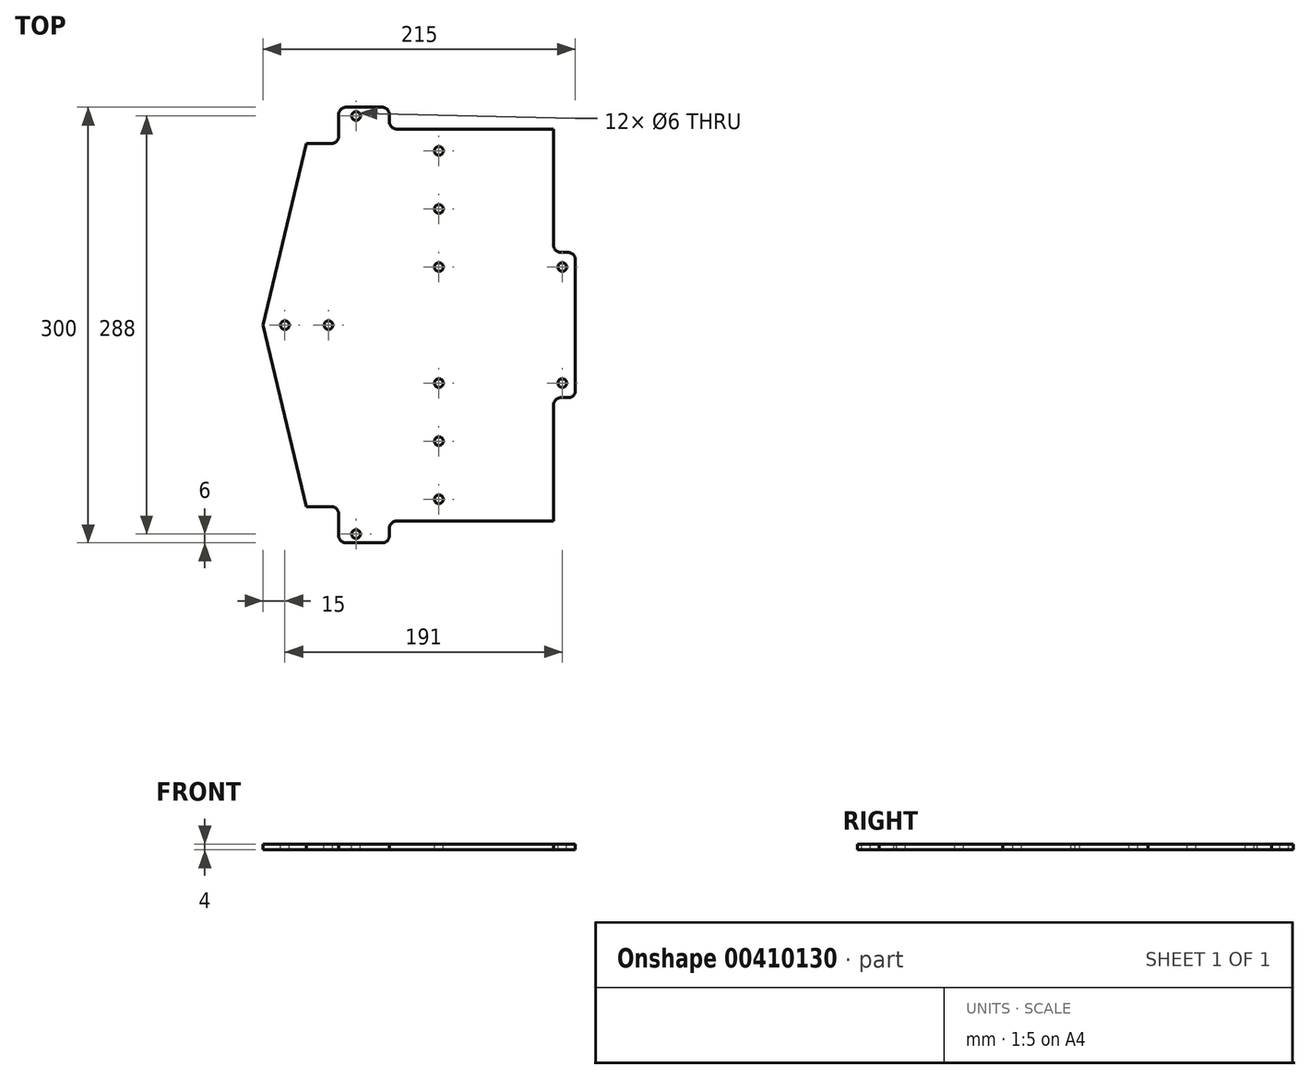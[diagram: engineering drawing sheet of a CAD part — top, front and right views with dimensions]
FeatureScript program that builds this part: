
annotation { "Feature Type Name" : "Feature", "Feature Type Description" : "" }
export const myFeature = defineFeature(function(context is Context, id is Id, definition is map)
    precondition{}
    {
        {
            var Q0;
            Q0=qCreatedBy(makeId("Top.planeOp"),FACE);
            var sketch = newSketch(context, id + "F0", { "sketchPlane" : qUnion([Q0])});
            skLineSegment(sketch, "E0.bottom", {"start": v(0, 0) * mm, "end": v(320, 0) * mm});
            skLineSegment(sketch, "E0.top", {"start": v(0, 420) * mm, "end": v(320, 420) * mm});
            skLineSegment(sketch, "E0.left", {"start": v(0, 0) * mm, "end": v(0, 420) * mm});
            skLineSegment(sketch, "E0.right", {"start": v(320, 0) * mm, "end": v(320, 420) * mm});
            skSolve(sketch);
        }
        {
            var Q0;
            Q0=qSketchRegion(id+"F0",true);
            extrude(context, id + "F1", {"entities" : qUnion([Q0]), "depth" : 4 * mm});
        }
        {
            var Q0;
            Q0=makeQuery(id+"F1.opExtrude","CAP_FACE",FACE,{"disambiguationData":[OSD([sQuery(id+"F0.wireOp",EDGE,"E0.bottom"),sQuery(id+"F0.wireOp",EDGE,"E0.top"),sQuery(id+"F0.wireOp",EDGE,"E0.left"),sQuery(id+"F0.wireOp",EDGE,"E0.right")])],"isStart":false});
            var sketch = newSketch(context, id + "F2", { "sketchPlane" : qUnion([Q0])});
            skLineSegment(sketch, "E1", {"start": v(290, 420) * mm, "end": v(320, 360) * mm});
            skLineSegment(sketch, "E2", {"start": v(290, 420) * mm, "end": v(320, 420) * mm});
            skLineSegment(sketch, "E3", {"start": v(320, 420) * mm, "end": v(320, 360) * mm});
            skLineSegment(sketch, "E4", {"start": v(290, 0) * mm, "end": v(320, 60) * mm});
            skLineSegment(sketch, "E5", {"start": v(290, 0) * mm, "end": v(320, 0) * mm});
            skLineSegment(sketch, "E6", {"start": v(320, 0) * mm, "end": v(320, 60) * mm});
            skLineSegment(sketch, "E7", {"start": v(0, 210) * mm, "end": v(320, 210) * mm, "construction": true});
            skLineSegment(sketch, "E8", {"start": v(163, 384) * mm, "end": v(163, 36) * mm, "construction": true});
            skPoint(sketch, "E9", {"position": v(163, 210) * mm});
            skLineSegment(sketch, "E10.bottom", {"start": v(213, 360) * mm, "end": v(113, 360) * mm});
            skLineSegment(sketch, "E10.top", {"start": v(213, 408) * mm, "end": v(113, 408) * mm});
            skLineSegment(sketch, "E10.left", {"start": v(218, 365) * mm, "end": v(218, 403) * mm});
            skLineSegment(sketch, "E10.right", {"start": v(108, 365) * mm, "end": v(108, 403) * mm});
            skPoint(sketch, "E10.middle", {"position": v(163, 384) * mm});
            skLineSegment(sketch, "E11.bottom", {"start": v(213, 12) * mm, "end": v(113, 12) * mm});
            skLineSegment(sketch, "E11.top", {"start": v(213, 60) * mm, "end": v(113, 60) * mm});
            skLineSegment(sketch, "E11.left", {"start": v(218, 17) * mm, "end": v(218, 55) * mm});
            skLineSegment(sketch, "E11.right", {"start": v(108, 17) * mm, "end": v(108, 55) * mm});
            skPoint(sketch, "E11.middle", {"position": v(163, 36) * mm});
            skPoint(sketch, "E12.visualSharp", {"position": v(108, 408) * mm});
            skArc(sketch, "E12.filletArc", {"start": v(113, 408) * mm, "mid": v(109.46, 406.54) * mm, "end": v(108, 403) * mm});
            skPoint(sketch, "E13.visualSharp", {"position": v(218, 408) * mm});
            skArc(sketch, "E13.filletArc", {"start": v(218, 403) * mm, "mid": v(216.54, 406.54) * mm, "end": v(213, 408) * mm});
            skPoint(sketch, "E14.visualSharp", {"position": v(108, 360) * mm});
            skArc(sketch, "E14.filletArc", {"start": v(108, 365) * mm, "mid": v(109.46, 361.46) * mm, "end": v(113, 360) * mm});
            skPoint(sketch, "E15.visualSharp", {"position": v(218, 360) * mm});
            skArc(sketch, "E15.filletArc", {"start": v(213, 360) * mm, "mid": v(216.54, 361.46) * mm, "end": v(218, 365) * mm});
            skPoint(sketch, "E16.visualSharp", {"position": v(218, 60) * mm});
            skArc(sketch, "E16.filletArc", {"start": v(218, 55) * mm, "mid": v(216.54, 58.54) * mm, "end": v(213, 60) * mm});
            skPoint(sketch, "E17.visualSharp", {"position": v(218, 12) * mm});
            skArc(sketch, "E17.filletArc", {"start": v(213, 12) * mm, "mid": v(216.54, 13.46) * mm, "end": v(218, 17) * mm});
            skPoint(sketch, "E18.visualSharp", {"position": v(108, 12) * mm});
            skArc(sketch, "E18.filletArc", {"start": v(108, 17) * mm, "mid": v(109.46, 13.46) * mm, "end": v(113, 12) * mm});
            skPoint(sketch, "E19.visualSharp", {"position": v(108, 60) * mm});
            skArc(sketch, "E19.filletArc", {"start": v(113, 60) * mm, "mid": v(109.46, 58.54) * mm, "end": v(108, 55) * mm});
            skLineSegment(sketch, "E20", {"start": v(0, 210) * mm, "end": v(50, 420) * mm});
            skLineSegment(sketch, "E21", {"start": v(0, 210) * mm, "end": v(50, 0) * mm});
            skLineSegment(sketch, "E22", {"start": v(50, 420) * mm, "end": v(0, 420) * mm});
            skLineSegment(sketch, "E23", {"start": v(0, 420) * mm, "end": v(0, 0) * mm});
            skLineSegment(sketch, "E24", {"start": v(0, 0) * mm, "end": v(50, 0) * mm});
            skSolve(sketch);
        }
        {
            var Q0;
            Q0=qSketchRegion(id+"F2",true);
            var Q1;
            Q1=makeQuery(id+"F1.opExtrude","CAP_FACE",FACE,{"disambiguationData":[OSD([sQuery(id+"F0.wireOp",EDGE,"E0.bottom"),sQuery(id+"F0.wireOp",EDGE,"E0.top"),sQuery(id+"F0.wireOp",EDGE,"E0.left"),sQuery(id+"F0.wireOp",EDGE,"E0.right")])],"isStart":true});
            extrude(context, id + "F3", {"entities" : qUnion([Q0]), "operationType" : NewBodyOperationType.REMOVE, "endBound" : BoundingType.UP_TO_SURFACE, "oppositeDirection" : true, "endBoundEntityFace" : qUnion([Q1]), "depth" : 25 * mm});
        }
        {
            var Q0;
            Q0=makeQuery(id+"F1.opExtrude","CAP_FACE",FACE,{"disambiguationData":[OSD([sQuery(id+"F0.wireOp",EDGE,"E0.bottom"),sQuery(id+"F0.wireOp",EDGE,"E0.top"),sQuery(id+"F0.wireOp",EDGE,"E0.left"),sQuery(id+"F0.wireOp",EDGE,"E0.right")])],"isStart":false});
            var sketch = newSketch(context, id + "F4", { "sketchPlane" : qUnion([Q0])});
            skLineSegment(sketch, "E25", {"start": v(67, 6) * mm, "end": v(277, 6) * mm, "construction": true});
            skCircle(sketch, "E26", {"center": v(67, 6) * mm, "radius": 3 * mm});
            skCircle(sketch, "E27.1.0.0", {"center": v(97, 6) * mm, "radius": 3 * mm});
            skCircle(sketch, "E27.2.0.0", {"center": v(127, 6) * mm, "radius": 3 * mm});
            skCircle(sketch, "E27.3.0.0", {"center": v(157, 6) * mm, "radius": 3 * mm});
            skCircle(sketch, "E27.4.0.0", {"center": v(187, 6) * mm, "radius": 3 * mm});
            skCircle(sketch, "E27.5.0.0", {"center": v(217, 6) * mm, "radius": 3 * mm});
            skCircle(sketch, "E27.6.0.0", {"center": v(247, 6) * mm, "radius": 3 * mm});
            skCircle(sketch, "E27.7.0.0", {"center": v(277, 6) * mm, "radius": 3 * mm});
            skLineSegment(sketch, "E27.direction1", {"start": v(67, 6) * mm, "end": v(97, 6) * mm, "construction": true});
            skLineSegment(sketch, "E28", {"start": v(70, 66) * mm, "end": v(310, 66) * mm, "construction": true});
            skCircle(sketch, "E29", {"center": v(64, 66) * mm, "radius": 3 * mm});
            skCircle(sketch, "E30.1.0.0", {"center": v(94, 66) * mm, "radius": 3 * mm});
            skCircle(sketch, "E30.2.0.0", {"center": v(124, 66) * mm, "radius": 3 * mm});
            skCircle(sketch, "E30.3.0.0", {"center": v(160, 66) * mm, "radius": 3 * mm, "construction": true});
            skCircle(sketch, "E30.4.0.0", {"center": v(190, 66) * mm, "radius": 3 * mm, "construction": true});
            skCircle(sketch, "E30.5.0.0", {"center": v(220, 66) * mm, "radius": 3 * mm});
            skCircle(sketch, "E30.6.0.0", {"center": v(250, 66) * mm, "radius": 3 * mm});
            skCircle(sketch, "E30.7.0.0", {"center": v(280, 66) * mm, "radius": 3 * mm});
            skCircle(sketch, "E30.8.0.0", {"center": v(310, 66) * mm, "radius": 3 * mm});
            skLineSegment(sketch, "E30.direction1", {"start": v(64, 66) * mm, "end": v(94, 66) * mm, "construction": true});
            skLineSegment(sketch, "E31", {"start": v(0, 210) * mm, "end": v(320, 210) * mm, "construction": true});
            skCircle(sketch, "E32.MirrorC", {"center": v(67, 414) * mm, "radius": 3 * mm});
            skCircle(sketch, "E33.MirrorC", {"center": v(64, 354) * mm, "radius": 3 * mm});
            skCircle(sketch, "E34.MirrorC", {"center": v(97, 414) * mm, "radius": 3 * mm});
            skCircle(sketch, "E35.MirrorC", {"center": v(310, 354) * mm, "radius": 3 * mm});
            skCircle(sketch, "E36.MirrorC", {"center": v(277, 414) * mm, "radius": 3 * mm});
            skCircle(sketch, "E37.MirrorC", {"center": v(94, 354) * mm, "radius": 3 * mm});
            skCircle(sketch, "E38.MirrorC", {"center": v(220, 354) * mm, "radius": 3 * mm});
            skLineSegment(sketch, "E39.MirrorCS", {"start": v(64, 354) * mm, "end": v(94, 354) * mm, "construction": true});
            skCircle(sketch, "E40.MirrorC", {"center": v(280, 354) * mm, "radius": 3 * mm});
            skCircle(sketch, "E41.MirrorC", {"center": v(124, 354) * mm, "radius": 3 * mm});
            skCircle(sketch, "E42.MirrorC", {"center": v(160, 354) * mm, "radius": 3 * mm, "construction": true});
            skCircle(sketch, "E43.MirrorC", {"center": v(190, 354) * mm, "radius": 3 * mm, "construction": true});
            skCircle(sketch, "E44.MirrorC", {"center": v(127, 414) * mm, "radius": 3 * mm});
            skCircle(sketch, "E45.MirrorC", {"center": v(250, 354) * mm, "radius": 3 * mm});
            skCircle(sketch, "E46.MirrorC", {"center": v(157, 414) * mm, "radius": 3 * mm});
            skCircle(sketch, "E47.MirrorC", {"center": v(187, 414) * mm, "radius": 3 * mm});
            skCircle(sketch, "E48.MirrorC", {"center": v(217, 414) * mm, "radius": 3 * mm});
            skCircle(sketch, "E49.MirrorC", {"center": v(247, 414) * mm, "radius": 3 * mm});
            skLineSegment(sketch, "E50.MirrorCS", {"start": v(67, 414) * mm, "end": v(277, 414) * mm, "construction": true});
            skLineSegment(sketch, "E51.MirrorCS", {"start": v(67, 414) * mm, "end": v(97, 414) * mm, "construction": true});
            skLineSegment(sketch, "E52.MirrorCS", {"start": v(70, 354) * mm, "end": v(310, 354) * mm, "construction": true});
            skSolve(sketch);
        }
        {
            var Q0;
            Q0=qSketchRegion(id+"F4",true);
            extrude(context, id + "F5", {"entities" : qUnion([Q0]), "operationType" : NewBodyOperationType.REMOVE, "oppositeDirection" : true, "depth" : 25 * mm});
        }
        {
            var Q0;
            Q0=makeQuery(id+"F1.opExtrude","CAP_FACE",FACE,{"disambiguationData":[OSD([sQuery(id+"F0.wireOp",EDGE,"E0.bottom"),sQuery(id+"F0.wireOp",EDGE,"E0.top"),sQuery(id+"F0.wireOp",EDGE,"E0.left"),sQuery(id+"F0.wireOp",EDGE,"E0.right")])],"isStart":false});
            var sketch = newSketch(context, id + "F6", { "sketchPlane" : qUnion([Q0])});
            skLineSegment(sketch, "E53", {"start": v(0, 210) * mm, "end": v(320, 210) * mm, "construction": true});
            skLineSegment(sketch, "E54", {"start": v(108, 365) * mm, "end": v(108, 55) * mm, "construction": true});
            skLineSegment(sketch, "E55", {"start": v(121, 90) * mm, "end": v(121, 330.2) * mm, "construction": true});
            skCircle(sketch, "E56", {"center": v(121, 90) * mm, "radius": 3 * mm});
            skCircle(sketch, "E57.0.1.0", {"center": v(121, 130) * mm, "radius": 3 * mm});
            skCircle(sketch, "E57.0.2.0", {"center": v(121, 170) * mm, "radius": 3 * mm});
            skCircle(sketch, "E57.1.0.0", {"center": v(206, 90) * mm, "radius": 3 * mm});
            skCircle(sketch, "E57.1.1.0", {"center": v(206, 130) * mm, "radius": 3 * mm});
            skCircle(sketch, "E57.1.2.0", {"center": v(206, 170) * mm, "radius": 3 * mm});
            skCircle(sketch, "E57.2.0.0", {"center": v(291, 80) * mm, "radius": 3 * mm});
            skCircle(sketch, "E57.2.1.0", {"center": v(291, 120) * mm, "radius": 3 * mm});
            skCircle(sketch, "E57.2.2.0", {"center": v(291, 160) * mm, "radius": 3 * mm});
            skLineSegment(sketch, "E57.direction1", {"start": v(121, 90) * mm, "end": v(206, 90) * mm, "construction": true});
            skLineSegment(sketch, "E57.direction2", {"start": v(121, 90) * mm, "end": v(121, 130) * mm, "construction": true});
            skCircle(sketch, "E58.MirrorC", {"center": v(121, 330) * mm, "radius": 3 * mm});
            skCircle(sketch, "E59.MirrorC", {"center": v(121, 290) * mm, "radius": 3 * mm});
            skCircle(sketch, "E60.MirrorC", {"center": v(206, 330) * mm, "radius": 3 * mm});
            skCircle(sketch, "E61.MirrorC", {"center": v(206, 250) * mm, "radius": 3 * mm});
            skCircle(sketch, "E62.MirrorC", {"center": v(291, 340) * mm, "radius": 3 * mm});
            skCircle(sketch, "E63.MirrorC", {"center": v(121, 250) * mm, "radius": 3 * mm});
            skCircle(sketch, "E64.MirrorC", {"center": v(206, 290) * mm, "radius": 3 * mm});
            skCircle(sketch, "E65.MirrorC", {"center": v(291, 300) * mm, "radius": 3 * mm});
            skCircle(sketch, "E66.MirrorC", {"center": v(291, 260) * mm, "radius": 3 * mm});
            skLineSegment(sketch, "E67.MirrorCS", {"start": v(121, 330) * mm, "end": v(121, 290) * mm, "construction": true});
            skLineSegment(sketch, "E68.MirrorCS", {"start": v(121, 330) * mm, "end": v(206, 330) * mm, "construction": true});
            skSolve(sketch);
        }
        {
            var Q0;
            Q0=qSketchRegion(id+"F6",true);
            extrude(context, id + "F7", {"entities" : qUnion([Q0]), "operationType" : NewBodyOperationType.REMOVE, "oppositeDirection" : true, "depth" : 25 * mm});
        }
        {
            var Q0;
            Q0=makeQuery(id+"F1.opExtrude","CAP_FACE",FACE,{"disambiguationData":[OSD([sQuery(id+"F0.wireOp",EDGE,"E0.bottom"),sQuery(id+"F0.wireOp",EDGE,"E0.top"),sQuery(id+"F0.wireOp",EDGE,"E0.left"),sQuery(id+"F0.wireOp",EDGE,"E0.right")])],"isStart":false});
            var sketch = newSketch(context, id + "F8", { "sketchPlane" : qUnion([Q0])});
            skLineSegment(sketch, "E69", {"start": v(0, 210) * mm, "end": v(320, 210) * mm, "construction": true});
            skCircle(sketch, "E70", {"center": v(15, 210) * mm, "radius": 3 * mm});
            skCircle(sketch, "E71.1.0.0", {"center": v(45, 210) * mm, "radius": 3 * mm});
            skLineSegment(sketch, "E71.direction1", {"start": v(15, 210) * mm, "end": v(45, 210) * mm, "construction": true});
            skSolve(sketch);
        }
        {
            var Q0;
            Q0=qSketchRegion(id+"F8",true);
            extrude(context, id + "F9", {"entities" : qUnion([Q0]), "operationType" : NewBodyOperationType.REMOVE, "oppositeDirection" : true, "depth" : 25 * mm});
        }
        {
            var Q0;
            Q0=makeQuery(id+"F1.opExtrude","CAP_FACE",FACE,{"disambiguationData":[OSD([sQuery(id+"F0.wireOp",EDGE,"E0.bottom"),sQuery(id+"F0.wireOp",EDGE,"E0.top"),sQuery(id+"F0.wireOp",EDGE,"E0.left"),sQuery(id+"F0.wireOp",EDGE,"E0.right")])],"isStart":false});
            var sketch = newSketch(context, id + "F10", { "sketchPlane" : qUnion([Q0])});
            skLineSegment(sketch, "E72", {"start": v(0, 210) * mm, "end": v(320, 210) * mm, "construction": true});
            skLineSegment(sketch, "E73.right", {"start": v(87, 355) * mm, "end": v(87, 350) * mm});
            skLineSegment(sketch, "E74", {"start": v(0, 335) * mm, "end": v(47, 335) * mm});
            skLineSegment(sketch, "E75", {"start": v(52, 340) * mm, "end": v(52, 355) * mm});
            skLineSegment(sketch, "E76", {"start": v(57, 360) * mm, "end": v(82, 360) * mm});
            skLineSegment(sketch, "E77", {"start": v(280, 340) * mm, "end": v(280, 338) * mm});
            skLineSegment(sketch, "E78", {"start": v(285, 333) * mm, "end": v(320, 333) * mm});
            skLineSegment(sketch, "E79", {"start": v(320, 333) * mm, "end": v(320, 210) * mm});
            skPoint(sketch, "E80.visualSharp", {"position": v(52, 335) * mm});
            skArc(sketch, "E80.filletArc", {"start": v(47, 335) * mm, "mid": v(50.54, 336.46) * mm, "end": v(52, 340) * mm});
            skPoint(sketch, "E81.newPointA", {"position": v(52, 360) * mm});
            skPoint(sketch, "E81.newPointB", {"position": v(0, 360) * mm});
            skArc(sketch, "E81.filletArc", {"start": v(57, 360) * mm, "mid": v(53.46, 358.54) * mm, "end": v(52, 355) * mm});
            skPoint(sketch, "E82.visualSharp", {"position": v(87, 360) * mm});
            skArc(sketch, "E82.filletArc", {"start": v(87, 355) * mm, "mid": v(85.54, 358.54) * mm, "end": v(82, 360) * mm});
            skArc(sketch, "E83.filletArc", {"start": v(87, 350) * mm, "mid": v(88.46, 346.46) * mm, "end": v(92, 345) * mm});
            skPoint(sketch, "E84.newPointA", {"position": v(280, 345) * mm});
            skPoint(sketch, "E84.newPointB", {"position": v(320, 345) * mm});
            skArc(sketch, "E84.filletArc", {"start": v(280, 340) * mm, "mid": v(278.54, 343.54) * mm, "end": v(275, 345) * mm});
            skPoint(sketch, "E85.visualSharp", {"position": v(280, 333) * mm});
            skArc(sketch, "E85.filletArc", {"start": v(280, 338) * mm, "mid": v(281.46, 334.46) * mm, "end": v(285, 333) * mm});
            skLineSegment(sketch, "E86", {"start": v(0, 335) * mm, "end": v(0, 210) * mm});
            skLineSegment(sketch, "E87", {"start": v(92, 345) * mm, "end": v(275, 345) * mm});
            skArc(sketch, "E88.MirrorCS", {"start": v(47, 85) * mm, "mid": v(50.54, 83.54) * mm, "end": v(52, 80) * mm});
            skArc(sketch, "E89.MirrorCS", {"start": v(87, 70) * mm, "mid": v(88.46, 73.54) * mm, "end": v(92, 75) * mm});
            skArc(sketch, "E90.MirrorCS", {"start": v(57, 60) * mm, "mid": v(53.46, 61.46) * mm, "end": v(52, 65) * mm});
            skLineSegment(sketch, "E91.MirrorCS", {"start": v(87, 65) * mm, "end": v(87, 70) * mm});
            skArc(sketch, "E92.MirrorCS", {"start": v(87, 65) * mm, "mid": v(85.54, 61.46) * mm, "end": v(82, 60) * mm});
            skLineSegment(sketch, "E93.MirrorCS", {"start": v(280, 80) * mm, "end": v(280, 82) * mm});
            skArc(sketch, "E94.MirrorCS", {"start": v(280, 82) * mm, "mid": v(281.46, 85.54) * mm, "end": v(285, 87) * mm});
            skArc(sketch, "E95.MirrorCS", {"start": v(280, 80) * mm, "mid": v(278.54, 76.46) * mm, "end": v(275, 75) * mm});
            skLineSegment(sketch, "E96.MirrorCS", {"start": v(52, 80) * mm, "end": v(52, 65) * mm});
            skLineSegment(sketch, "E97.MirrorCS", {"start": v(57, 60) * mm, "end": v(82, 60) * mm});
            skPoint(sketch, "E98.MirrorP", {"position": v(320, 75) * mm});
            skLineSegment(sketch, "E99.MirrorCS", {"start": v(320, 87) * mm, "end": v(320, 210) * mm});
            skPoint(sketch, "E100.MirrorP", {"position": v(52, 60) * mm});
            skPoint(sketch, "E101.MirrorP", {"position": v(52, 85) * mm});
            skPoint(sketch, "E102.MirrorP", {"position": v(87, 60) * mm});
            skPoint(sketch, "E103.MirrorP", {"position": v(280, 87) * mm});
            skLineSegment(sketch, "E104.MirrorCS", {"start": v(92, 75) * mm, "end": v(275, 75) * mm});
            skPoint(sketch, "E105.MirrorP", {"position": v(0, 60) * mm});
            skLineSegment(sketch, "E106.MirrorCS", {"start": v(0, 85) * mm, "end": v(0, 210) * mm});
            skLineSegment(sketch, "E107.MirrorCS", {"start": v(285, 87) * mm, "end": v(320, 87) * mm});
            skPoint(sketch, "E108.MirrorP", {"position": v(280, 75) * mm});
            skLineSegment(sketch, "E109.MirrorCS", {"start": v(0, 85) * mm, "end": v(47, 85) * mm});
            skSolve(sketch);
        }
        {
            var Q0;
            Q0=qSketchRegion(id+"F10",true);
            extrude(context, id + "F11", {"entities" : qUnion([Q0]), "operationType" : NewBodyOperationType.INTERSECT, "oppositeDirection" : true, "depth" : 25 * mm});
        }
        {
            var Q0;
            Q0=makeQuery(id+"F1.opExtrude","CAP_FACE",FACE,{"disambiguationData":[OSD([sQuery(id+"F0.wireOp",EDGE,"E0.bottom"),sQuery(id+"F0.wireOp",EDGE,"E0.top"),sQuery(id+"F0.wireOp",EDGE,"E0.left"),sQuery(id+"F0.wireOp",EDGE,"E0.right")])],"isStart":false});
            var sketch = newSketch(context, id + "F12", { "sketchPlane" : qUnion([Q0])});
            skPoint(sketch, "E110.oppositeSnap0", {"position": v(200, 345) * mm});
            skLineSegment(sketch, "E110.bottom", {"start": v(320, 345) * mm, "end": v(200, 345) * mm});
            skLineSegment(sketch, "E110.top", {"start": v(320, 75) * mm, "end": v(200, 75) * mm});
            skLineSegment(sketch, "E110.left", {"start": v(320, 345) * mm, "end": v(320, 75) * mm});
            skLineSegment(sketch, "E111", {"start": v(0, 210) * mm, "end": v(320, 210) * mm, "construction": true});
            skLineSegment(sketch, "E112.bottom", {"start": v(210, 160) * mm, "end": v(205, 160) * mm});
            skLineSegment(sketch, "E112.top", {"start": v(210, 260) * mm, "end": v(205, 260) * mm});
            skLineSegment(sketch, "E112.left", {"start": v(215, 165) * mm, "end": v(215, 255) * mm});
            skPoint(sketch, "E112.middle", {"position": v(200, 210) * mm});
            skPoint(sketch, "E113.orphan", {"position": v(185, 260) * mm});
            skPoint(sketch, "E114.orphan", {"position": v(185, 160) * mm});
            skLineSegment(sketch, "E115.trimOffspring", {"start": v(200, 155) * mm, "end": v(200, 75) * mm});
            skLineSegment(sketch, "E116", {"start": v(200, 345) * mm, "end": v(200, 265) * mm});
            skPoint(sketch, "E117", {"position": v(215, 210) * mm});
            skPoint(sketch, "E118.visualSharp", {"position": v(200, 260) * mm});
            skArc(sketch, "E118.filletArc", {"start": v(200, 265) * mm, "mid": v(201.46, 261.46) * mm, "end": v(205, 260) * mm});
            skPoint(sketch, "E119.visualSharp", {"position": v(215, 260) * mm});
            skArc(sketch, "E119.filletArc", {"start": v(215, 255) * mm, "mid": v(213.54, 258.54) * mm, "end": v(210, 260) * mm});
            skPoint(sketch, "E120.visualSharp", {"position": v(215, 160) * mm});
            skArc(sketch, "E120.filletArc", {"start": v(210, 160) * mm, "mid": v(213.54, 161.46) * mm, "end": v(215, 165) * mm});
            skPoint(sketch, "E121.visualSharp", {"position": v(200, 160) * mm});
            skArc(sketch, "E121.filletArc", {"start": v(205, 160) * mm, "mid": v(201.46, 158.54) * mm, "end": v(200, 155) * mm});
            skSolve(sketch);
        }
        {
            var Q0;
            Q0 = qSketchRegion(id + "F12", true);
            extrude(context, id + "F13", {"entities" : qUnion([Q0]), "operationType" : NewBodyOperationType.REMOVE, "oppositeDirection" : true, "depth" : 25 * mm});
        }
    });
